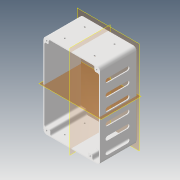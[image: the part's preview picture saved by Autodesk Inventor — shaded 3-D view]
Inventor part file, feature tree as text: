
AUTODESK INVENTOR PART (.ipt)
format: ipt  version: 2022 (Build 260153000, 153)  size: 240,640 bytes
history: native  units: mm
features: plane x5, sketch x3, extrude x2, other x2, fillet x1, pattern_linear x1, hole x1, reference x1, projected_geometry x1
ambient origin geometry x8: Origin, YZ Plane, XZ Plane, XY Plane, X Axis, Y Axis, Z Axis, Center Point
bodies: Volumenkörper1 (feature_tree)
feature tree (17):
  plane  "Arbeitsebene1"
  sketch  "Skizze1"  dims[d0=1.5mm d1=3.0mm d2=3.0mm]
  plane  "Arbeitsebene2"
  extrude  "Extrusion1"  Depth=3.0mm
  fillet  "Rundung1"  Radius=3.0mm
  extrude  "Extrusion4"  Depth=7.0mm
  pattern_linear  "Rechteckige Anordnung2"  Spacing1=7.0mm  [1 undecoded]
  plane  "Arbeitsebene3"
  plane  "Arbeitsebene4"
  hole  "Bohrung1"  [1 undecoded]
  plane  "Arbeitsebene5"
  reference  "Referenz1"
  sketch  "Skizze4"  dims[d3=55.0mm d4=0.0mm d5=7.0mm]
  sketch  "Skizze5"  dims[d6=7.0mm d7=7.0mm d8=7.0mm d9=10.0mm d10=2.8mm d13=2.0mm d29=6.0mm d30=55.0mm d31=0.0mm d32=60.0mm d34=18.9mm d35=45.0mm d36=30.0mm d37=2.8mm d38=6.0mm d39=4.0mm d40=2.0mm d41=90.0deg d42=8.0mm d43=20.594885mm]
  projected_geometry  "Projizierte Kontur2"
  other  "Omniscope_new_v0.iam"
  other  "Omniscope_Base_v0:1"
note: 2 required parameter values undecoded (feature->parameter linkage not recoverable at this tier; creation-order binding heuristic only, values carry confidence <= 0.55)
